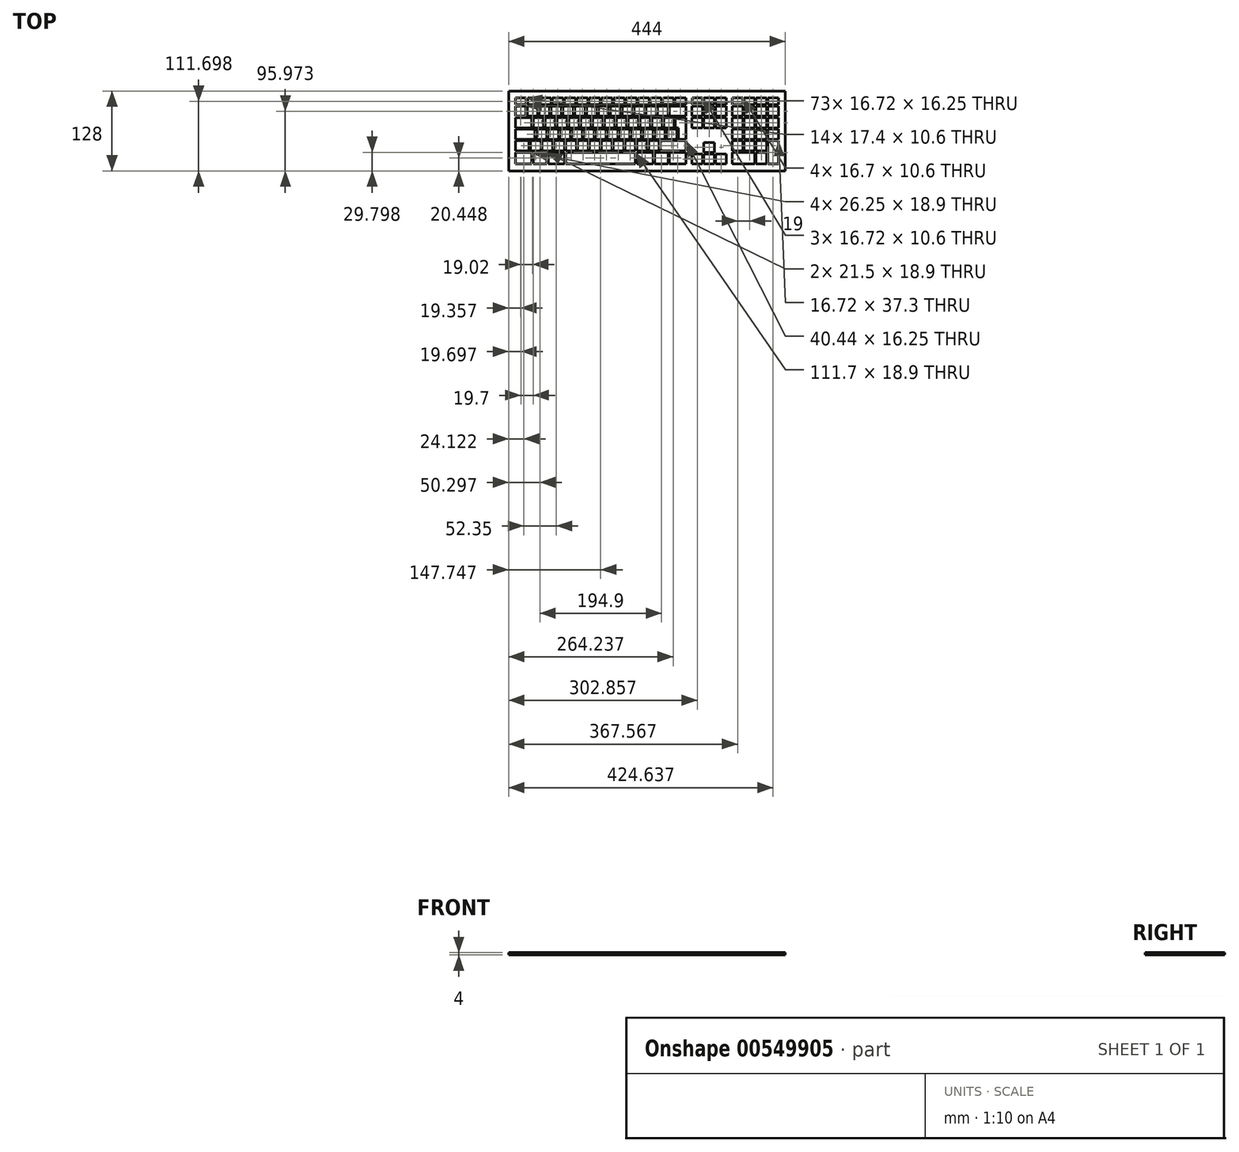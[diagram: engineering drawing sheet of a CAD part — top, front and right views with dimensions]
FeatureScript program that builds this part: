
annotation { "Feature Type Name" : "Feature", "Feature Type Description" : "" }
export const myFeature = defineFeature(function(context is Context, id is Id, definition is map)
    precondition{}
    {
        {
            var Q0;
            Q0=qCreatedBy(makeId("Top.planeOp"),FACE);
            var sketch = newSketch(context, id + "F0", { "sketchPlane" : qUnion([Q0])});
            skLineSegment(sketch, "E0.bottom", {"start": v(-207.41, -87.25) * mm, "end": v(222.59, -87.25) * mm, "construction": true});
            skLineSegment(sketch, "E0.top", {"start": v(-207.41, -201.25) * mm, "end": v(222.59, -201.25) * mm, "construction": true});
            skLineSegment(sketch, "E0.left", {"start": v(-207.41, -87.25) * mm, "end": v(-207.41, -201.25) * mm, "construction": true});
            skLineSegment(sketch, "E0.right", {"start": v(222.59, -87.25) * mm, "end": v(222.59, -201.25) * mm, "construction": true});
            skLineSegment(sketch, "E1.bottom", {"start": v(-203.41, -91.25) * mm, "end": v(-186.01, -91.25) * mm});
            skLineSegment(sketch, "E1.top", {"start": v(-203.41, -101.85) * mm, "end": v(-186.01, -101.85) * mm});
            skLineSegment(sketch, "E1.left", {"start": v(-203.41, -91.25) * mm, "end": v(-203.41, -101.85) * mm});
            skLineSegment(sketch, "E1.right", {"start": v(-186.01, -91.25) * mm, "end": v(-186.01, -101.85) * mm});
            skPoint(sketch, "E1.middle", {"position": v(-194.71, -96.55) * mm});
            skLineSegment(sketch, "E2.1.0.0", {"start": v(-166.31, -91.25) * mm, "end": v(-166.31, -101.85) * mm});
            skPoint(sketch, "E2.1.0.1", {"position": v(-175.01, -96.55) * mm});
            skLineSegment(sketch, "E2.1.0.2", {"start": v(-183.71, -91.25) * mm, "end": v(-183.71, -101.85) * mm});
            skLineSegment(sketch, "E2.1.0.3", {"start": v(-183.71, -101.85) * mm, "end": v(-166.31, -101.85) * mm});
            skLineSegment(sketch, "E2.1.0.4", {"start": v(-183.71, -91.25) * mm, "end": v(-166.31, -91.25) * mm});
            skLineSegment(sketch, "E2.2.0.0", {"start": v(-146.61, -91.25) * mm, "end": v(-146.61, -101.85) * mm});
            skPoint(sketch, "E2.2.0.1", {"position": v(-155.31, -96.55) * mm});
            skLineSegment(sketch, "E2.2.0.2", {"start": v(-164.01, -91.25) * mm, "end": v(-164.01, -101.85) * mm});
            skLineSegment(sketch, "E2.2.0.3", {"start": v(-164.01, -101.85) * mm, "end": v(-146.61, -101.85) * mm});
            skLineSegment(sketch, "E2.2.0.4", {"start": v(-164.01, -91.25) * mm, "end": v(-146.61, -91.25) * mm});
            skLineSegment(sketch, "E2.3.0.0", {"start": v(-126.91, -91.25) * mm, "end": v(-126.91, -101.85) * mm});
            skPoint(sketch, "E2.3.0.1", {"position": v(-135.61, -96.55) * mm});
            skLineSegment(sketch, "E2.3.0.2", {"start": v(-144.31, -91.25) * mm, "end": v(-144.31, -101.85) * mm});
            skLineSegment(sketch, "E2.3.0.3", {"start": v(-144.31, -101.85) * mm, "end": v(-126.91, -101.85) * mm});
            skLineSegment(sketch, "E2.3.0.4", {"start": v(-144.31, -91.25) * mm, "end": v(-126.91, -91.25) * mm});
            skLineSegment(sketch, "E2.4.0.0", {"start": v(-107.21, -91.25) * mm, "end": v(-107.21, -101.85) * mm});
            skPoint(sketch, "E2.4.0.1", {"position": v(-115.91, -96.55) * mm});
            skLineSegment(sketch, "E2.4.0.2", {"start": v(-124.61, -91.25) * mm, "end": v(-124.61, -101.85) * mm});
            skLineSegment(sketch, "E2.4.0.3", {"start": v(-124.61, -101.85) * mm, "end": v(-107.21, -101.85) * mm});
            skLineSegment(sketch, "E2.4.0.4", {"start": v(-124.61, -91.25) * mm, "end": v(-107.21, -91.25) * mm});
            skLineSegment(sketch, "E2.5.0.0", {"start": v(-87.51, -91.25) * mm, "end": v(-87.51, -101.85) * mm});
            skPoint(sketch, "E2.5.0.1", {"position": v(-96.21, -96.55) * mm});
            skLineSegment(sketch, "E2.5.0.2", {"start": v(-104.91, -91.25) * mm, "end": v(-104.91, -101.85) * mm});
            skLineSegment(sketch, "E2.5.0.3", {"start": v(-104.91, -101.85) * mm, "end": v(-87.51, -101.85) * mm});
            skLineSegment(sketch, "E2.5.0.4", {"start": v(-104.91, -91.25) * mm, "end": v(-87.51, -91.25) * mm});
            skLineSegment(sketch, "E2.6.0.0", {"start": v(-67.81, -91.25) * mm, "end": v(-67.81, -101.85) * mm});
            skPoint(sketch, "E2.6.0.1", {"position": v(-76.51, -96.55) * mm});
            skLineSegment(sketch, "E2.6.0.2", {"start": v(-85.21, -91.25) * mm, "end": v(-85.21, -101.85) * mm});
            skLineSegment(sketch, "E2.6.0.3", {"start": v(-85.21, -101.85) * mm, "end": v(-67.81, -101.85) * mm});
            skLineSegment(sketch, "E2.6.0.4", {"start": v(-85.21, -91.25) * mm, "end": v(-67.81, -91.25) * mm});
            skLineSegment(sketch, "E2.7.0.0", {"start": v(-48.11, -91.25) * mm, "end": v(-48.11, -101.85) * mm});
            skPoint(sketch, "E2.7.0.1", {"position": v(-56.81, -96.55) * mm});
            skLineSegment(sketch, "E2.7.0.2", {"start": v(-65.51, -91.25) * mm, "end": v(-65.51, -101.85) * mm});
            skLineSegment(sketch, "E2.7.0.3", {"start": v(-65.51, -101.85) * mm, "end": v(-48.11, -101.85) * mm});
            skLineSegment(sketch, "E2.7.0.4", {"start": v(-65.51, -91.25) * mm, "end": v(-48.11, -91.25) * mm});
            skLineSegment(sketch, "E2.8.0.0", {"start": v(-28.41, -91.25) * mm, "end": v(-28.41, -101.85) * mm});
            skPoint(sketch, "E2.8.0.1", {"position": v(-37.11, -96.55) * mm});
            skLineSegment(sketch, "E2.8.0.2", {"start": v(-45.81, -91.25) * mm, "end": v(-45.81, -101.85) * mm});
            skLineSegment(sketch, "E2.8.0.3", {"start": v(-45.81, -101.85) * mm, "end": v(-28.41, -101.85) * mm});
            skLineSegment(sketch, "E2.8.0.4", {"start": v(-45.81, -91.25) * mm, "end": v(-28.41, -91.25) * mm});
            skLineSegment(sketch, "E2.9.0.0", {"start": v(-8.71, -91.25) * mm, "end": v(-8.71, -101.85) * mm});
            skPoint(sketch, "E2.9.0.1", {"position": v(-17.41, -96.55) * mm});
            skLineSegment(sketch, "E2.9.0.2", {"start": v(-26.11, -91.25) * mm, "end": v(-26.11, -101.85) * mm});
            skLineSegment(sketch, "E2.9.0.3", {"start": v(-26.11, -101.85) * mm, "end": v(-8.71, -101.85) * mm});
            skLineSegment(sketch, "E2.9.0.4", {"start": v(-26.11, -91.25) * mm, "end": v(-8.71, -91.25) * mm});
            skLineSegment(sketch, "E2.10.0.0", {"start": v(10.99, -91.25) * mm, "end": v(10.99, -101.85) * mm});
            skPoint(sketch, "E2.10.0.1", {"position": v(2.29, -96.55) * mm});
            skLineSegment(sketch, "E2.10.0.2", {"start": v(-6.41, -91.25) * mm, "end": v(-6.41, -101.85) * mm});
            skLineSegment(sketch, "E2.10.0.3", {"start": v(-6.41, -101.85) * mm, "end": v(10.99, -101.85) * mm});
            skLineSegment(sketch, "E2.10.0.4", {"start": v(-6.41, -91.25) * mm, "end": v(10.99, -91.25) * mm});
            skLineSegment(sketch, "E2.11.0.0", {"start": v(30.69, -91.25) * mm, "end": v(30.69, -101.85) * mm});
            skPoint(sketch, "E2.11.0.1", {"position": v(21.99, -96.55) * mm});
            skLineSegment(sketch, "E2.11.0.2", {"start": v(13.29, -91.25) * mm, "end": v(13.29, -101.85) * mm});
            skLineSegment(sketch, "E2.11.0.3", {"start": v(13.29, -101.85) * mm, "end": v(30.69, -101.85) * mm});
            skLineSegment(sketch, "E2.11.0.4", {"start": v(13.29, -91.25) * mm, "end": v(30.69, -91.25) * mm});
            skLineSegment(sketch, "E2.12.0.0", {"start": v(50.39, -91.25) * mm, "end": v(50.39, -101.85) * mm});
            skPoint(sketch, "E2.12.0.1", {"position": v(41.69, -96.55) * mm});
            skLineSegment(sketch, "E2.12.0.2", {"start": v(32.99, -91.25) * mm, "end": v(32.99, -101.85) * mm});
            skLineSegment(sketch, "E2.12.0.3", {"start": v(32.99, -101.85) * mm, "end": v(50.39, -101.85) * mm});
            skLineSegment(sketch, "E2.12.0.4", {"start": v(32.99, -91.25) * mm, "end": v(50.39, -91.25) * mm});
            skLineSegment(sketch, "E2.13.0.0", {"start": v(70.09, -91.25) * mm, "end": v(70.09, -101.85) * mm});
            skPoint(sketch, "E2.13.0.1", {"position": v(61.39, -96.55) * mm});
            skLineSegment(sketch, "E2.13.0.2", {"start": v(52.69, -91.25) * mm, "end": v(52.69, -101.85) * mm});
            skLineSegment(sketch, "E2.13.0.3", {"start": v(52.69, -101.85) * mm, "end": v(70.09, -101.85) * mm});
            skLineSegment(sketch, "E2.13.0.4", {"start": v(52.69, -91.25) * mm, "end": v(70.09, -91.25) * mm});
            skLineSegment(sketch, "E3.bottom", {"start": v(80.09, -91.25) * mm, "end": v(96.8, -91.25) * mm});
            skLineSegment(sketch, "E3.top", {"start": v(80.09, -101.85) * mm, "end": v(96.8, -101.85) * mm});
            skLineSegment(sketch, "E3.left", {"start": v(80.09, -91.25) * mm, "end": v(80.09, -101.85) * mm});
            skLineSegment(sketch, "E3.right", {"start": v(96.8, -91.25) * mm, "end": v(96.8, -101.85) * mm});
            skPoint(sketch, "E3.middle", {"position": v(88.45, -96.55) * mm});
            skLineSegment(sketch, "E4.1.0.0", {"start": v(115.8, -91.25) * mm, "end": v(115.8, -101.85) * mm});
            skLineSegment(sketch, "E4.1.0.1", {"start": v(99.09, -91.25) * mm, "end": v(99.09, -101.85) * mm});
            skLineSegment(sketch, "E4.1.0.2", {"start": v(99.09, -91.25) * mm, "end": v(115.8, -91.25) * mm});
            skPoint(sketch, "E4.1.0.3", {"position": v(107.45, -96.55) * mm});
            skLineSegment(sketch, "E4.1.0.4", {"start": v(99.09, -101.85) * mm, "end": v(115.8, -101.85) * mm});
            skLineSegment(sketch, "E4.2.0.0", {"start": v(134.8, -91.25) * mm, "end": v(134.8, -101.85) * mm});
            skLineSegment(sketch, "E4.2.0.1", {"start": v(118.09, -91.25) * mm, "end": v(118.09, -101.85) * mm});
            skLineSegment(sketch, "E4.2.0.2", {"start": v(118.09, -91.25) * mm, "end": v(134.8, -91.25) * mm});
            skPoint(sketch, "E4.2.0.3", {"position": v(126.45, -96.55) * mm});
            skLineSegment(sketch, "E4.2.0.4", {"start": v(118.09, -101.85) * mm, "end": v(134.8, -101.85) * mm});
            skLineSegment(sketch, "E5.bottom", {"start": v(144.8, -91.25) * mm, "end": v(161.5, -91.25) * mm});
            skLineSegment(sketch, "E5.top", {"start": v(144.8, -101.85) * mm, "end": v(161.5, -101.85) * mm});
            skLineSegment(sketch, "E5.left", {"start": v(144.8, -91.25) * mm, "end": v(144.8, -101.85) * mm});
            skLineSegment(sketch, "E5.right", {"start": v(161.5, -91.25) * mm, "end": v(161.5, -101.85) * mm});
            skPoint(sketch, "E5.middle", {"position": v(153.16, -96.55) * mm});
            skLineSegment(sketch, "E6.1.0.0", {"start": v(180.5, -91.25) * mm, "end": v(180.5, -101.85) * mm});
            skLineSegment(sketch, "E6.1.0.1", {"start": v(163.8, -91.25) * mm, "end": v(180.5, -91.25) * mm});
            skLineSegment(sketch, "E6.1.0.2", {"start": v(163.8, -101.85) * mm, "end": v(180.5, -101.85) * mm});
            skLineSegment(sketch, "E6.1.0.3", {"start": v(163.8, -91.25) * mm, "end": v(163.8, -101.85) * mm});
            skPoint(sketch, "E6.1.0.4", {"position": v(172.16, -96.55) * mm});
            skLineSegment(sketch, "E6.2.0.0", {"start": v(199.5, -91.25) * mm, "end": v(199.5, -101.85) * mm});
            skLineSegment(sketch, "E6.2.0.1", {"start": v(182.8, -91.25) * mm, "end": v(199.5, -91.25) * mm});
            skLineSegment(sketch, "E6.2.0.2", {"start": v(182.8, -101.85) * mm, "end": v(199.5, -101.85) * mm});
            skLineSegment(sketch, "E6.2.0.3", {"start": v(182.8, -91.25) * mm, "end": v(182.8, -101.85) * mm});
            skPoint(sketch, "E6.2.0.4", {"position": v(191.16, -96.55) * mm});
            skLineSegment(sketch, "E6.3.0.0", {"start": v(218.5, -91.25) * mm, "end": v(218.5, -101.85) * mm});
            skLineSegment(sketch, "E6.3.0.1", {"start": v(201.8, -91.25) * mm, "end": v(218.5, -91.25) * mm});
            skLineSegment(sketch, "E6.3.0.2", {"start": v(201.8, -101.85) * mm, "end": v(218.5, -101.85) * mm});
            skLineSegment(sketch, "E6.3.0.3", {"start": v(201.8, -91.25) * mm, "end": v(201.8, -101.85) * mm});
            skPoint(sketch, "E6.3.0.4", {"position": v(210.16, -96.55) * mm});
            skLineSegment(sketch, "E7.bottom", {"start": v(-203.41, -104.15) * mm, "end": v(-186.7, -104.15) * mm});
            skLineSegment(sketch, "E7.top", {"start": v(-203.41, -120.4) * mm, "end": v(-186.7, -120.4) * mm});
            skLineSegment(sketch, "E7.left", {"start": v(-203.41, -104.15) * mm, "end": v(-203.41, -120.4) * mm});
            skLineSegment(sketch, "E7.right", {"start": v(-186.7, -104.15) * mm, "end": v(-186.7, -120.4) * mm});
            skPoint(sketch, "E7.middle", {"position": v(-195.05, -112.28) * mm});
            skPoint(sketch, "E8.1.0.0", {"position": v(-176.03, -112.28) * mm});
            skLineSegment(sketch, "E8.1.0.1", {"start": v(-167.67, -104.15) * mm, "end": v(-167.67, -120.4) * mm});
            skLineSegment(sketch, "E8.1.0.2", {"start": v(-184.4, -104.15) * mm, "end": v(-167.67, -104.15) * mm});
            skLineSegment(sketch, "E8.1.0.3", {"start": v(-184.4, -104.15) * mm, "end": v(-184.4, -120.4) * mm});
            skLineSegment(sketch, "E8.1.0.4", {"start": v(-184.4, -120.4) * mm, "end": v(-167.67, -120.4) * mm});
            skPoint(sketch, "E8.2.0.0", {"position": v(-157.01, -112.28) * mm});
            skLineSegment(sketch, "E8.2.0.1", {"start": v(-148.65, -104.15) * mm, "end": v(-148.65, -120.4) * mm});
            skLineSegment(sketch, "E8.2.0.2", {"start": v(-165.37, -104.15) * mm, "end": v(-148.65, -104.15) * mm});
            skLineSegment(sketch, "E8.2.0.3", {"start": v(-165.37, -104.15) * mm, "end": v(-165.37, -120.4) * mm});
            skLineSegment(sketch, "E8.2.0.4", {"start": v(-165.37, -120.4) * mm, "end": v(-148.65, -120.4) * mm});
            skPoint(sketch, "E8.3.0.0", {"position": v(-138, -112.28) * mm});
            skLineSegment(sketch, "E8.3.0.1", {"start": v(-129.63, -104.15) * mm, "end": v(-129.63, -120.4) * mm});
            skLineSegment(sketch, "E8.3.0.2", {"start": v(-146.35, -104.15) * mm, "end": v(-129.63, -104.15) * mm});
            skLineSegment(sketch, "E8.3.0.3", {"start": v(-146.35, -104.15) * mm, "end": v(-146.35, -120.4) * mm});
            skLineSegment(sketch, "E8.3.0.4", {"start": v(-146.35, -120.4) * mm, "end": v(-129.63, -120.4) * mm});
            skPoint(sketch, "E8.4.0.0", {"position": v(-118.97, -112.28) * mm});
            skLineSegment(sketch, "E8.4.0.1", {"start": v(-110.61, -104.15) * mm, "end": v(-110.61, -120.4) * mm});
            skLineSegment(sketch, "E8.4.0.2", {"start": v(-127.33, -104.15) * mm, "end": v(-110.61, -104.15) * mm});
            skLineSegment(sketch, "E8.4.0.3", {"start": v(-127.33, -104.15) * mm, "end": v(-127.33, -120.4) * mm});
            skLineSegment(sketch, "E8.4.0.4", {"start": v(-127.33, -120.4) * mm, "end": v(-110.61, -120.4) * mm});
            skPoint(sketch, "E8.5.0.0", {"position": v(-99.95, -112.28) * mm});
            skLineSegment(sketch, "E8.5.0.1", {"start": v(-91.6, -104.15) * mm, "end": v(-91.6, -120.4) * mm});
            skLineSegment(sketch, "E8.5.0.2", {"start": v(-108.31, -104.15) * mm, "end": v(-91.6, -104.15) * mm});
            skLineSegment(sketch, "E8.5.0.3", {"start": v(-108.31, -104.15) * mm, "end": v(-108.31, -120.4) * mm});
            skLineSegment(sketch, "E8.5.0.4", {"start": v(-108.31, -120.4) * mm, "end": v(-91.6, -120.4) * mm});
            skPoint(sketch, "E8.6.0.0", {"position": v(-80.93, -112.28) * mm});
            skLineSegment(sketch, "E8.6.0.1", {"start": v(-72.57, -104.15) * mm, "end": v(-72.57, -120.4) * mm});
            skLineSegment(sketch, "E8.6.0.2", {"start": v(-89.3, -104.15) * mm, "end": v(-72.57, -104.15) * mm});
            skLineSegment(sketch, "E8.6.0.3", {"start": v(-89.3, -104.15) * mm, "end": v(-89.3, -120.4) * mm});
            skLineSegment(sketch, "E8.6.0.4", {"start": v(-89.3, -120.4) * mm, "end": v(-72.57, -120.4) * mm});
            skPoint(sketch, "E8.7.0.0", {"position": v(-61.91, -112.28) * mm});
            skLineSegment(sketch, "E8.7.0.1", {"start": v(-53.55, -104.15) * mm, "end": v(-53.55, -120.4) * mm});
            skLineSegment(sketch, "E8.7.0.2", {"start": v(-70.27, -104.15) * mm, "end": v(-53.55, -104.15) * mm});
            skLineSegment(sketch, "E8.7.0.3", {"start": v(-70.27, -104.15) * mm, "end": v(-70.27, -120.4) * mm});
            skLineSegment(sketch, "E8.7.0.4", {"start": v(-70.27, -120.4) * mm, "end": v(-53.55, -120.4) * mm});
            skPoint(sketch, "E8.8.0.0", {"position": v(-42.9, -112.28) * mm});
            skLineSegment(sketch, "E8.8.0.1", {"start": v(-34.53, -104.15) * mm, "end": v(-34.53, -120.4) * mm});
            skLineSegment(sketch, "E8.8.0.2", {"start": v(-51.25, -104.15) * mm, "end": v(-34.53, -104.15) * mm});
            skLineSegment(sketch, "E8.8.0.3", {"start": v(-51.25, -104.15) * mm, "end": v(-51.25, -120.4) * mm});
            skLineSegment(sketch, "E8.8.0.4", {"start": v(-51.25, -120.4) * mm, "end": v(-34.53, -120.4) * mm});
            skPoint(sketch, "E8.9.0.0", {"position": v(-23.87, -112.28) * mm});
            skLineSegment(sketch, "E8.9.0.1", {"start": v(-15.51, -104.15) * mm, "end": v(-15.51, -120.4) * mm});
            skLineSegment(sketch, "E8.9.0.2", {"start": v(-32.23, -104.15) * mm, "end": v(-15.51, -104.15) * mm});
            skLineSegment(sketch, "E8.9.0.3", {"start": v(-32.23, -104.15) * mm, "end": v(-32.23, -120.4) * mm});
            skLineSegment(sketch, "E8.9.0.4", {"start": v(-32.23, -120.4) * mm, "end": v(-15.51, -120.4) * mm});
            skPoint(sketch, "E8.10.0.0", {"position": v(-4.85, -112.28) * mm});
            skLineSegment(sketch, "E8.10.0.1", {"start": v(3.5, -104.15) * mm, "end": v(3.5, -120.4) * mm});
            skLineSegment(sketch, "E8.10.0.2", {"start": v(-13.21, -104.15) * mm, "end": v(3.5, -104.15) * mm});
            skLineSegment(sketch, "E8.10.0.3", {"start": v(-13.21, -104.15) * mm, "end": v(-13.21, -120.4) * mm});
            skLineSegment(sketch, "E8.10.0.4", {"start": v(-13.21, -120.4) * mm, "end": v(3.5, -120.4) * mm});
            skPoint(sketch, "E8.11.0.0", {"position": v(14.17, -112.28) * mm});
            skLineSegment(sketch, "E8.11.0.1", {"start": v(22.53, -104.15) * mm, "end": v(22.53, -120.4) * mm});
            skLineSegment(sketch, "E8.11.0.2", {"start": v(5.8, -104.15) * mm, "end": v(22.53, -104.15) * mm});
            skLineSegment(sketch, "E8.11.0.3", {"start": v(5.8, -104.15) * mm, "end": v(5.8, -120.4) * mm});
            skLineSegment(sketch, "E8.11.0.4", {"start": v(5.8, -120.4) * mm, "end": v(22.53, -120.4) * mm});
            skPoint(sketch, "E8.12.0.0", {"position": v(33.19, -112.28) * mm});
            skLineSegment(sketch, "E8.12.0.1", {"start": v(41.55, -104.15) * mm, "end": v(41.55, -120.4) * mm});
            skLineSegment(sketch, "E8.12.0.2", {"start": v(24.83, -104.15) * mm, "end": v(41.55, -104.15) * mm});
            skLineSegment(sketch, "E8.12.0.3", {"start": v(24.83, -104.15) * mm, "end": v(24.83, -120.4) * mm});
            skLineSegment(sketch, "E8.12.0.4", {"start": v(24.83, -120.4) * mm, "end": v(41.55, -120.4) * mm});
            skLineSegment(sketch, "E9.bottom", {"start": v(43.85, -104.15) * mm, "end": v(70.05, -104.15) * mm});
            skLineSegment(sketch, "E9.top", {"start": v(43.85, -120.4) * mm, "end": v(70.05, -120.4) * mm});
            skLineSegment(sketch, "E9.left", {"start": v(43.85, -104.15) * mm, "end": v(43.85, -120.4) * mm});
            skLineSegment(sketch, "E9.right", {"start": v(70.05, -104.15) * mm, "end": v(70.05, -120.4) * mm});
            skPoint(sketch, "E9.middle", {"position": v(56.95, -112.28) * mm});
            skLineSegment(sketch, "E10.bottom", {"start": v(80.05, -104.15) * mm, "end": v(96.77, -104.15) * mm});
            skLineSegment(sketch, "E10.top", {"start": v(80.05, -120.4) * mm, "end": v(96.77, -120.4) * mm});
            skLineSegment(sketch, "E10.left", {"start": v(80.05, -104.15) * mm, "end": v(80.05, -120.4) * mm});
            skLineSegment(sketch, "E10.right", {"start": v(96.77, -104.15) * mm, "end": v(96.77, -120.4) * mm});
            skPoint(sketch, "E10.middle", {"position": v(88.4, -112.28) * mm});
            skPoint(sketch, "E11.1.0.0", {"position": v(107.43, -112.28) * mm});
            skLineSegment(sketch, "E11.1.0.1", {"start": v(99.07, -120.4) * mm, "end": v(115.79, -120.4) * mm});
            skLineSegment(sketch, "E11.1.0.2", {"start": v(115.79, -104.15) * mm, "end": v(115.79, -120.4) * mm});
            skLineSegment(sketch, "E11.1.0.3", {"start": v(99.07, -104.15) * mm, "end": v(115.79, -104.15) * mm});
            skLineSegment(sketch, "E11.1.0.4", {"start": v(99.07, -104.15) * mm, "end": v(99.07, -120.4) * mm});
            skPoint(sketch, "E11.2.0.0", {"position": v(126.45, -112.28) * mm});
            skLineSegment(sketch, "E11.2.0.1", {"start": v(118.09, -120.4) * mm, "end": v(134.8, -120.4) * mm});
            skLineSegment(sketch, "E11.2.0.2", {"start": v(134.8, -104.15) * mm, "end": v(134.8, -120.4) * mm});
            skLineSegment(sketch, "E11.2.0.3", {"start": v(118.09, -104.15) * mm, "end": v(134.8, -104.15) * mm});
            skLineSegment(sketch, "E11.2.0.4", {"start": v(118.09, -104.15) * mm, "end": v(118.09, -120.4) * mm});
            skLineSegment(sketch, "E12.bottom", {"start": v(80.05, -122.7) * mm, "end": v(96.77, -122.7) * mm});
            skLineSegment(sketch, "E12.top", {"start": v(80.05, -138.95) * mm, "end": v(96.77, -138.95) * mm});
            skLineSegment(sketch, "E12.left", {"start": v(80.05, -122.7) * mm, "end": v(80.05, -138.95) * mm});
            skLineSegment(sketch, "E12.right", {"start": v(96.77, -122.7) * mm, "end": v(96.77, -138.95) * mm});
            skPoint(sketch, "E12.middle", {"position": v(88.4, -130.83) * mm});
            skLineSegment(sketch, "E13.1.0.0", {"start": v(99.07, -138.95) * mm, "end": v(115.79, -138.95) * mm});
            skLineSegment(sketch, "E13.1.0.1", {"start": v(99.07, -122.7) * mm, "end": v(115.79, -122.7) * mm});
            skLineSegment(sketch, "E13.1.0.2", {"start": v(99.07, -122.7) * mm, "end": v(99.07, -138.95) * mm});
            skPoint(sketch, "E13.1.0.3", {"position": v(107.43, -130.83) * mm});
            skLineSegment(sketch, "E13.1.0.4", {"start": v(115.79, -122.7) * mm, "end": v(115.79, -138.95) * mm});
            skLineSegment(sketch, "E13.2.0.0", {"start": v(118.09, -138.95) * mm, "end": v(134.8, -138.95) * mm});
            skLineSegment(sketch, "E13.2.0.1", {"start": v(118.09, -122.7) * mm, "end": v(134.8, -122.7) * mm});
            skLineSegment(sketch, "E13.2.0.2", {"start": v(118.09, -122.7) * mm, "end": v(118.09, -138.95) * mm});
            skPoint(sketch, "E13.2.0.3", {"position": v(126.45, -130.83) * mm});
            skLineSegment(sketch, "E13.2.0.4", {"start": v(134.8, -122.7) * mm, "end": v(134.8, -138.95) * mm});
            skPoint(sketch, "E14.1.0.0", {"position": v(153.17, -112.28) * mm});
            skLineSegment(sketch, "E14.1.0.1", {"start": v(144.8, -104.15) * mm, "end": v(161.53, -104.15) * mm});
            skLineSegment(sketch, "E14.1.0.3", {"start": v(161.53, -104.15) * mm, "end": v(161.53, -120.4) * mm});
            skLineSegment(sketch, "E14.1.0.4", {"start": v(144.8, -120.4) * mm, "end": v(161.53, -120.4) * mm});
            skLineSegment(sketch, "E14.1.0.7", {"start": v(144.8, -104.15) * mm, "end": v(144.8, -120.4) * mm});
            skLineSegment(sketch, "E15.0.1.0", {"start": v(144.8, -122.7) * mm, "end": v(144.8, -138.95) * mm});
            skPoint(sketch, "E15.0.1.1", {"position": v(153.17, -130.83) * mm});
            skLineSegment(sketch, "E15.0.1.2", {"start": v(144.8, -122.7) * mm, "end": v(161.53, -122.7) * mm});
            skLineSegment(sketch, "E15.0.1.3", {"start": v(161.53, -122.7) * mm, "end": v(161.53, -138.95) * mm});
            skLineSegment(sketch, "E15.0.1.4", {"start": v(144.8, -138.95) * mm, "end": v(161.53, -138.95) * mm});
            skLineSegment(sketch, "E15.0.2.0", {"start": v(144.8, -141.25) * mm, "end": v(144.8, -157.5) * mm});
            skPoint(sketch, "E15.0.2.1", {"position": v(153.17, -149.38) * mm});
            skLineSegment(sketch, "E15.0.2.2", {"start": v(144.8, -141.25) * mm, "end": v(161.53, -141.25) * mm});
            skLineSegment(sketch, "E15.0.2.3", {"start": v(161.53, -141.25) * mm, "end": v(161.53, -157.5) * mm});
            skLineSegment(sketch, "E15.0.2.4", {"start": v(144.8, -157.5) * mm, "end": v(161.53, -157.5) * mm});
            skLineSegment(sketch, "E15.0.3.0", {"start": v(144.8, -159.8) * mm, "end": v(144.8, -176.05) * mm});
            skPoint(sketch, "E15.0.3.1", {"position": v(153.17, -167.93) * mm});
            skLineSegment(sketch, "E15.0.3.2", {"start": v(144.8, -159.8) * mm, "end": v(161.53, -159.8) * mm});
            skLineSegment(sketch, "E15.0.3.3", {"start": v(161.53, -159.8) * mm, "end": v(161.53, -176.05) * mm});
            skLineSegment(sketch, "E15.0.3.4", {"start": v(144.8, -176.05) * mm, "end": v(161.53, -176.05) * mm});
            skLineSegment(sketch, "E15.1.0.0", {"start": v(163.83, -104.15) * mm, "end": v(163.83, -120.4) * mm});
            skPoint(sketch, "E15.1.0.1", {"position": v(172.19, -112.28) * mm});
            skLineSegment(sketch, "E15.1.0.2", {"start": v(163.83, -104.15) * mm, "end": v(180.55, -104.15) * mm});
            skLineSegment(sketch, "E15.1.0.3", {"start": v(180.55, -104.15) * mm, "end": v(180.55, -120.4) * mm});
            skLineSegment(sketch, "E15.1.0.4", {"start": v(163.83, -120.4) * mm, "end": v(180.55, -120.4) * mm});
            skLineSegment(sketch, "E15.1.1.0", {"start": v(163.83, -122.7) * mm, "end": v(163.83, -138.95) * mm});
            skPoint(sketch, "E15.1.1.1", {"position": v(172.19, -130.83) * mm});
            skLineSegment(sketch, "E15.1.1.2", {"start": v(163.83, -122.7) * mm, "end": v(180.55, -122.7) * mm});
            skLineSegment(sketch, "E15.1.1.3", {"start": v(180.55, -122.7) * mm, "end": v(180.55, -138.95) * mm});
            skLineSegment(sketch, "E15.1.1.4", {"start": v(163.83, -138.95) * mm, "end": v(180.55, -138.95) * mm});
            skLineSegment(sketch, "E15.1.2.0", {"start": v(163.83, -141.25) * mm, "end": v(163.83, -157.5) * mm});
            skPoint(sketch, "E15.1.2.1", {"position": v(172.19, -149.38) * mm});
            skLineSegment(sketch, "E15.1.2.2", {"start": v(163.83, -141.25) * mm, "end": v(180.55, -141.25) * mm});
            skLineSegment(sketch, "E15.1.2.3", {"start": v(180.55, -141.25) * mm, "end": v(180.55, -157.5) * mm});
            skLineSegment(sketch, "E15.1.2.4", {"start": v(163.83, -157.5) * mm, "end": v(180.55, -157.5) * mm});
            skLineSegment(sketch, "E15.1.3.0", {"start": v(163.83, -159.8) * mm, "end": v(163.83, -176.05) * mm});
            skPoint(sketch, "E15.1.3.1", {"position": v(172.19, -167.93) * mm});
            skLineSegment(sketch, "E15.1.3.2", {"start": v(163.83, -159.8) * mm, "end": v(180.55, -159.8) * mm});
            skLineSegment(sketch, "E15.1.3.3", {"start": v(180.55, -159.8) * mm, "end": v(180.55, -176.05) * mm});
            skLineSegment(sketch, "E15.1.3.4", {"start": v(163.83, -176.05) * mm, "end": v(180.55, -176.05) * mm});
            skLineSegment(sketch, "E15.2.0.0", {"start": v(182.85, -104.15) * mm, "end": v(182.85, -120.4) * mm});
            skPoint(sketch, "E15.2.0.1", {"position": v(191.2, -112.28) * mm});
            skLineSegment(sketch, "E15.2.0.2", {"start": v(182.85, -104.15) * mm, "end": v(199.57, -104.15) * mm});
            skLineSegment(sketch, "E15.2.0.3", {"start": v(199.57, -104.15) * mm, "end": v(199.57, -120.4) * mm});
            skLineSegment(sketch, "E15.2.0.4", {"start": v(182.85, -120.4) * mm, "end": v(199.57, -120.4) * mm});
            skLineSegment(sketch, "E15.2.1.0", {"start": v(182.85, -122.7) * mm, "end": v(182.85, -138.95) * mm});
            skPoint(sketch, "E15.2.1.1", {"position": v(191.2, -130.83) * mm});
            skLineSegment(sketch, "E15.2.1.2", {"start": v(182.85, -122.7) * mm, "end": v(199.57, -122.7) * mm});
            skLineSegment(sketch, "E15.2.1.3", {"start": v(199.57, -122.7) * mm, "end": v(199.57, -138.95) * mm});
            skLineSegment(sketch, "E15.2.1.4", {"start": v(182.85, -138.95) * mm, "end": v(199.57, -138.95) * mm});
            skLineSegment(sketch, "E15.2.2.0", {"start": v(182.85, -141.25) * mm, "end": v(182.85, -157.5) * mm});
            skPoint(sketch, "E15.2.2.1", {"position": v(191.2, -149.38) * mm});
            skLineSegment(sketch, "E15.2.2.2", {"start": v(182.85, -141.25) * mm, "end": v(199.57, -141.25) * mm});
            skLineSegment(sketch, "E15.2.2.3", {"start": v(199.57, -141.25) * mm, "end": v(199.57, -157.5) * mm});
            skLineSegment(sketch, "E15.2.2.4", {"start": v(182.85, -157.5) * mm, "end": v(199.57, -157.5) * mm});
            skLineSegment(sketch, "E15.2.3.0", {"start": v(182.85, -159.8) * mm, "end": v(182.85, -176.05) * mm});
            skPoint(sketch, "E15.2.3.1", {"position": v(191.2, -167.93) * mm});
            skLineSegment(sketch, "E15.2.3.2", {"start": v(182.85, -159.8) * mm, "end": v(199.57, -159.8) * mm});
            skLineSegment(sketch, "E15.2.3.3", {"start": v(199.57, -159.8) * mm, "end": v(199.57, -176.05) * mm});
            skLineSegment(sketch, "E15.2.3.4", {"start": v(182.85, -176.05) * mm, "end": v(199.57, -176.05) * mm});
            skLineSegment(sketch, "E15.3.0.0", {"start": v(201.87, -104.15) * mm, "end": v(201.87, -120.4) * mm});
            skPoint(sketch, "E15.3.0.1", {"position": v(210.23, -112.28) * mm});
            skLineSegment(sketch, "E15.3.0.2", {"start": v(201.87, -104.15) * mm, "end": v(218.59, -104.15) * mm});
            skLineSegment(sketch, "E15.3.0.3", {"start": v(218.59, -104.15) * mm, "end": v(218.59, -120.4) * mm});
            skLineSegment(sketch, "E15.3.0.4", {"start": v(201.87, -120.4) * mm, "end": v(218.59, -120.4) * mm});
            skLineSegment(sketch, "E15.3.1.0", {"start": v(201.87, -122.7) * mm, "end": v(201.87, -138.95) * mm});
            skPoint(sketch, "E15.3.1.1", {"position": v(210.23, -130.83) * mm});
            skLineSegment(sketch, "E15.3.1.2", {"start": v(201.87, -122.7) * mm, "end": v(218.59, -122.7) * mm});
            skLineSegment(sketch, "E15.3.1.3", {"start": v(218.59, -122.7) * mm, "end": v(218.59, -138.95) * mm});
            skLineSegment(sketch, "E15.3.1.4", {"start": v(201.87, -138.95) * mm, "end": v(218.59, -138.95) * mm});
            skLineSegment(sketch, "E15.3.2.0", {"start": v(201.87, -141.25) * mm, "end": v(201.87, -157.5) * mm});
            skPoint(sketch, "E15.3.2.1", {"position": v(210.23, -149.38) * mm});
            skLineSegment(sketch, "E15.3.2.2", {"start": v(201.87, -141.25) * mm, "end": v(218.59, -141.25) * mm});
            skLineSegment(sketch, "E15.3.2.3", {"start": v(218.59, -141.25) * mm, "end": v(218.59, -157.5) * mm});
            skLineSegment(sketch, "E15.3.2.4", {"start": v(201.87, -157.5) * mm, "end": v(218.59, -157.5) * mm});
            skLineSegment(sketch, "E15.3.3.0", {"start": v(201.87, -159.8) * mm, "end": v(201.87, -197.1) * mm});
            skPoint(sketch, "E15.3.3.1", {"position": v(210.23, -178.45) * mm});
            skLineSegment(sketch, "E15.3.3.2", {"start": v(201.87, -159.8) * mm, "end": v(218.59, -159.8) * mm});
            skLineSegment(sketch, "E15.3.3.3", {"start": v(218.59, -159.8) * mm, "end": v(218.59, -197.1) * mm});
            skLineSegment(sketch, "E15.3.3.4", {"start": v(201.87, -197.1) * mm, "end": v(218.59, -197.1) * mm});
            skLineSegment(sketch, "E16.bottom", {"start": v(182.85, -178.35) * mm, "end": v(199.57, -178.35) * mm});
            skLineSegment(sketch, "E16.top", {"start": v(182.85, -197.16) * mm, "end": v(199.57, -197.16) * mm});
            skLineSegment(sketch, "E16.left", {"start": v(182.85, -178.35) * mm, "end": v(182.85, -197.16) * mm});
            skLineSegment(sketch, "E16.right", {"start": v(199.57, -178.35) * mm, "end": v(199.57, -197.16) * mm});
            skPoint(sketch, "E16.middle", {"position": v(191.2, -187.76) * mm});
            skLineSegment(sketch, "E17.bottom", {"start": v(144.8, -178.35) * mm, "end": v(180.55, -178.35) * mm});
            skLineSegment(sketch, "E17.top", {"start": v(144.8, -197.16) * mm, "end": v(180.55, -197.16) * mm});
            skLineSegment(sketch, "E17.left", {"start": v(144.8, -178.35) * mm, "end": v(144.8, -197.16) * mm});
            skLineSegment(sketch, "E17.right", {"start": v(180.55, -178.35) * mm, "end": v(180.55, -197.16) * mm});
            skPoint(sketch, "E17.middle", {"position": v(162.68, -187.76) * mm});
            skLineSegment(sketch, "E18.bottom", {"start": v(118.09, -181) * mm, "end": v(134.8, -181) * mm});
            skLineSegment(sketch, "E18.top", {"start": v(118.09, -197.25) * mm, "end": v(134.8, -197.25) * mm});
            skLineSegment(sketch, "E18.left", {"start": v(118.09, -181) * mm, "end": v(118.09, -197.25) * mm});
            skLineSegment(sketch, "E18.right", {"start": v(134.8, -181) * mm, "end": v(134.8, -197.25) * mm});
            skPoint(sketch, "E18.middle", {"position": v(126.45, -189.13) * mm});
            skPoint(sketch, "E19.1.0.0", {"position": v(107.43, -189.13) * mm});
            skLineSegment(sketch, "E19.1.0.1", {"start": v(99.07, -197.25) * mm, "end": v(115.79, -197.25) * mm});
            skLineSegment(sketch, "E19.1.0.2", {"start": v(99.07, -181) * mm, "end": v(115.79, -181) * mm});
            skLineSegment(sketch, "E19.1.0.3", {"start": v(115.79, -181) * mm, "end": v(115.79, -197.25) * mm});
            skLineSegment(sketch, "E19.1.0.4", {"start": v(99.07, -181) * mm, "end": v(99.07, -197.25) * mm});
            skPoint(sketch, "E19.2.0.0", {"position": v(88.4, -189.13) * mm});
            skLineSegment(sketch, "E19.2.0.1", {"start": v(80.05, -197.25) * mm, "end": v(96.77, -197.25) * mm});
            skLineSegment(sketch, "E19.2.0.2", {"start": v(80.05, -181) * mm, "end": v(96.77, -181) * mm});
            skLineSegment(sketch, "E19.2.0.3", {"start": v(96.77, -181) * mm, "end": v(96.77, -197.25) * mm});
            skLineSegment(sketch, "E19.2.0.4", {"start": v(80.05, -181) * mm, "end": v(80.05, -197.25) * mm});
            skLineSegment(sketch, "E20.0.1.0", {"start": v(99.07, -162.45) * mm, "end": v(115.79, -162.45) * mm});
            skLineSegment(sketch, "E20.0.1.1", {"start": v(99.07, -162.45) * mm, "end": v(99.07, -178.7) * mm});
            skLineSegment(sketch, "E20.0.1.2", {"start": v(115.79, -162.45) * mm, "end": v(115.79, -178.7) * mm});
            skPoint(sketch, "E20.0.1.3", {"position": v(107.43, -170.58) * mm});
            skLineSegment(sketch, "E20.0.1.4", {"start": v(99.07, -178.7) * mm, "end": v(115.79, -178.7) * mm});
            skLineSegment(sketch, "E21.bottom", {"start": v(-203.41, -122.7) * mm, "end": v(-177.16, -122.7) * mm});
            skLineSegment(sketch, "E21.top", {"start": v(-203.41, -138.95) * mm, "end": v(-177.16, -138.95) * mm});
            skLineSegment(sketch, "E21.left", {"start": v(-203.41, -122.7) * mm, "end": v(-203.41, -138.95) * mm});
            skLineSegment(sketch, "E21.right", {"start": v(-177.16, -122.7) * mm, "end": v(-177.16, -138.95) * mm});
            skPoint(sketch, "E21.middle", {"position": v(-190.29, -130.83) * mm});
            skLineSegment(sketch, "E22.bottom", {"start": v(-174.86, -122.7) * mm, "end": v(-158.14, -122.7) * mm});
            skLineSegment(sketch, "E22.top", {"start": v(-174.86, -138.95) * mm, "end": v(-158.14, -138.95) * mm});
            skLineSegment(sketch, "E22.left", {"start": v(-174.86, -122.7) * mm, "end": v(-174.86, -138.95) * mm});
            skLineSegment(sketch, "E22.right", {"start": v(-158.14, -122.7) * mm, "end": v(-158.14, -138.95) * mm});
            skPoint(sketch, "E22.middle", {"position": v(-166.5, -130.83) * mm});
            skLineSegment(sketch, "E23.1.0.0", {"start": v(-139.12, -122.7) * mm, "end": v(-139.12, -138.95) * mm});
            skLineSegment(sketch, "E23.1.0.1", {"start": v(-155.84, -122.7) * mm, "end": v(-155.84, -138.95) * mm});
            skLineSegment(sketch, "E23.1.0.2", {"start": v(-155.84, -122.7) * mm, "end": v(-139.12, -122.7) * mm});
            skPoint(sketch, "E23.1.0.3", {"position": v(-147.48, -130.83) * mm});
            skLineSegment(sketch, "E23.1.0.4", {"start": v(-155.84, -138.95) * mm, "end": v(-139.12, -138.95) * mm});
            skLineSegment(sketch, "E23.2.0.0", {"start": v(-120.1, -122.7) * mm, "end": v(-120.1, -138.95) * mm});
            skLineSegment(sketch, "E23.2.0.1", {"start": v(-136.82, -122.7) * mm, "end": v(-136.82, -138.95) * mm});
            skLineSegment(sketch, "E23.2.0.2", {"start": v(-136.82, -122.7) * mm, "end": v(-120.1, -122.7) * mm});
            skPoint(sketch, "E23.2.0.3", {"position": v(-128.46, -130.83) * mm});
            skLineSegment(sketch, "E23.2.0.4", {"start": v(-136.82, -138.95) * mm, "end": v(-120.1, -138.95) * mm});
            skLineSegment(sketch, "E23.3.0.0", {"start": v(-101.08, -122.7) * mm, "end": v(-101.08, -138.95) * mm});
            skLineSegment(sketch, "E23.3.0.1", {"start": v(-117.8, -122.7) * mm, "end": v(-117.8, -138.95) * mm});
            skLineSegment(sketch, "E23.3.0.2", {"start": v(-117.8, -122.7) * mm, "end": v(-101.08, -122.7) * mm});
            skPoint(sketch, "E23.3.0.3", {"position": v(-109.44, -130.83) * mm});
            skLineSegment(sketch, "E23.3.0.4", {"start": v(-117.8, -138.95) * mm, "end": v(-101.08, -138.95) * mm});
            skLineSegment(sketch, "E23.4.0.0", {"start": v(-82.06, -122.7) * mm, "end": v(-82.06, -138.95) * mm});
            skLineSegment(sketch, "E23.4.0.1", {"start": v(-98.78, -122.7) * mm, "end": v(-98.78, -138.95) * mm});
            skLineSegment(sketch, "E23.4.0.2", {"start": v(-98.78, -122.7) * mm, "end": v(-82.06, -122.7) * mm});
            skPoint(sketch, "E23.4.0.3", {"position": v(-90.42, -130.83) * mm});
            skLineSegment(sketch, "E23.4.0.4", {"start": v(-98.78, -138.95) * mm, "end": v(-82.06, -138.95) * mm});
            skLineSegment(sketch, "E23.5.0.0", {"start": v(-63.04, -122.7) * mm, "end": v(-63.04, -138.95) * mm});
            skLineSegment(sketch, "E23.5.0.1", {"start": v(-79.76, -122.7) * mm, "end": v(-79.76, -138.95) * mm});
            skLineSegment(sketch, "E23.5.0.2", {"start": v(-79.76, -122.7) * mm, "end": v(-63.04, -122.7) * mm});
            skPoint(sketch, "E23.5.0.3", {"position": v(-71.4, -130.83) * mm});
            skLineSegment(sketch, "E23.5.0.4", {"start": v(-79.76, -138.95) * mm, "end": v(-63.04, -138.95) * mm});
            skLineSegment(sketch, "E23.6.0.0", {"start": v(-44.02, -122.7) * mm, "end": v(-44.02, -138.95) * mm});
            skLineSegment(sketch, "E23.6.0.1", {"start": v(-60.74, -122.7) * mm, "end": v(-60.74, -138.95) * mm});
            skLineSegment(sketch, "E23.6.0.2", {"start": v(-60.74, -122.7) * mm, "end": v(-44.02, -122.7) * mm});
            skPoint(sketch, "E23.6.0.3", {"position": v(-52.38, -130.83) * mm});
            skLineSegment(sketch, "E23.6.0.4", {"start": v(-60.74, -138.95) * mm, "end": v(-44.02, -138.95) * mm});
            skLineSegment(sketch, "E23.7.0.0", {"start": v(-25, -122.7) * mm, "end": v(-25, -138.95) * mm});
            skLineSegment(sketch, "E23.7.0.1", {"start": v(-41.72, -122.7) * mm, "end": v(-41.72, -138.95) * mm});
            skLineSegment(sketch, "E23.7.0.2", {"start": v(-41.72, -122.7) * mm, "end": v(-25, -122.7) * mm});
            skPoint(sketch, "E23.7.0.3", {"position": v(-33.36, -130.83) * mm});
            skLineSegment(sketch, "E23.7.0.4", {"start": v(-41.72, -138.95) * mm, "end": v(-25, -138.95) * mm});
            skLineSegment(sketch, "E23.8.0.0", {"start": v(-5.98, -122.7) * mm, "end": v(-5.98, -138.95) * mm});
            skLineSegment(sketch, "E23.8.0.1", {"start": v(-22.7, -122.7) * mm, "end": v(-22.7, -138.95) * mm});
            skLineSegment(sketch, "E23.8.0.2", {"start": v(-22.7, -122.7) * mm, "end": v(-5.98, -122.7) * mm});
            skPoint(sketch, "E23.8.0.3", {"position": v(-14.34, -130.83) * mm});
            skLineSegment(sketch, "E23.8.0.4", {"start": v(-22.7, -138.95) * mm, "end": v(-5.98, -138.95) * mm});
            skLineSegment(sketch, "E23.9.0.0", {"start": v(13.04, -122.7) * mm, "end": v(13.04, -138.95) * mm});
            skLineSegment(sketch, "E23.9.0.1", {"start": v(-3.68, -122.7) * mm, "end": v(-3.68, -138.95) * mm});
            skLineSegment(sketch, "E23.9.0.2", {"start": v(-3.68, -122.7) * mm, "end": v(13.04, -122.7) * mm});
            skPoint(sketch, "E23.9.0.3", {"position": v(4.68, -130.83) * mm});
            skLineSegment(sketch, "E23.9.0.4", {"start": v(-3.68, -138.95) * mm, "end": v(13.04, -138.95) * mm});
            skLineSegment(sketch, "E23.10.0.0", {"start": v(32.06, -122.7) * mm, "end": v(32.06, -138.95) * mm});
            skLineSegment(sketch, "E23.10.0.1", {"start": v(15.34, -122.7) * mm, "end": v(15.34, -138.95) * mm});
            skLineSegment(sketch, "E23.10.0.2", {"start": v(15.34, -122.7) * mm, "end": v(32.06, -122.7) * mm});
            skPoint(sketch, "E23.10.0.3", {"position": v(23.7, -130.83) * mm});
            skLineSegment(sketch, "E23.10.0.4", {"start": v(15.34, -138.95) * mm, "end": v(32.06, -138.95) * mm});
            skLineSegment(sketch, "E23.11.0.0", {"start": v(51.08, -122.7) * mm, "end": v(51.08, -138.95) * mm});
            skLineSegment(sketch, "E23.11.0.1", {"start": v(34.36, -122.7) * mm, "end": v(34.36, -138.95) * mm});
            skLineSegment(sketch, "E23.11.0.2", {"start": v(34.36, -122.7) * mm, "end": v(51.08, -122.7) * mm});
            skPoint(sketch, "E23.11.0.3", {"position": v(42.72, -130.83) * mm});
            skLineSegment(sketch, "E23.11.0.4", {"start": v(34.36, -138.95) * mm, "end": v(51.08, -138.95) * mm});
            skLineSegment(sketch, "E24.bottom", {"start": v(-203.41, -141.25) * mm, "end": v(-172.41, -141.25) * mm});
            skLineSegment(sketch, "E24.top", {"start": v(-203.41, -157.5) * mm, "end": v(-172.41, -157.5) * mm});
            skLineSegment(sketch, "E24.left", {"start": v(-203.41, -141.25) * mm, "end": v(-203.41, -157.5) * mm});
            skLineSegment(sketch, "E24.right", {"start": v(-172.41, -141.25) * mm, "end": v(-172.41, -157.5) * mm});
            skPoint(sketch, "E24.middle", {"position": v(-187.91, -149.38) * mm});
            skLineSegment(sketch, "E25.bottom", {"start": v(-170.11, -141.25) * mm, "end": v(-153.4, -141.25) * mm});
            skLineSegment(sketch, "E25.top", {"start": v(-170.11, -157.5) * mm, "end": v(-153.4, -157.5) * mm});
            skLineSegment(sketch, "E25.left", {"start": v(-170.11, -141.25) * mm, "end": v(-170.11, -157.5) * mm});
            skLineSegment(sketch, "E25.right", {"start": v(-153.4, -141.25) * mm, "end": v(-153.4, -157.5) * mm});
            skPoint(sketch, "E25.middle", {"position": v(-161.75, -149.38) * mm});
            skLineSegment(sketch, "E26.1.0.0", {"start": v(-151.1, -157.5) * mm, "end": v(-134.37, -157.5) * mm});
            skPoint(sketch, "E26.1.0.1", {"position": v(-142.73, -149.38) * mm});
            skLineSegment(sketch, "E26.1.0.2", {"start": v(-151.1, -141.25) * mm, "end": v(-134.37, -141.25) * mm});
            skLineSegment(sketch, "E26.1.0.3", {"start": v(-134.37, -141.25) * mm, "end": v(-134.37, -157.5) * mm});
            skLineSegment(sketch, "E26.1.0.4", {"start": v(-151.1, -141.25) * mm, "end": v(-151.1, -157.5) * mm});
            skLineSegment(sketch, "E26.2.0.0", {"start": v(-132.07, -157.5) * mm, "end": v(-115.35, -157.5) * mm});
            skPoint(sketch, "E26.2.0.1", {"position": v(-123.71, -149.38) * mm});
            skLineSegment(sketch, "E26.2.0.2", {"start": v(-132.07, -141.25) * mm, "end": v(-115.35, -141.25) * mm});
            skLineSegment(sketch, "E26.2.0.3", {"start": v(-115.35, -141.25) * mm, "end": v(-115.35, -157.5) * mm});
            skLineSegment(sketch, "E26.2.0.4", {"start": v(-132.07, -141.25) * mm, "end": v(-132.07, -157.5) * mm});
            skLineSegment(sketch, "E26.3.0.0", {"start": v(-113.05, -157.5) * mm, "end": v(-96.33, -157.5) * mm});
            skPoint(sketch, "E26.3.0.1", {"position": v(-104.7, -149.38) * mm});
            skLineSegment(sketch, "E26.3.0.2", {"start": v(-113.05, -141.25) * mm, "end": v(-96.33, -141.25) * mm});
            skLineSegment(sketch, "E26.3.0.3", {"start": v(-96.33, -141.25) * mm, "end": v(-96.33, -157.5) * mm});
            skLineSegment(sketch, "E26.3.0.4", {"start": v(-113.05, -141.25) * mm, "end": v(-113.05, -157.5) * mm});
            skLineSegment(sketch, "E26.4.0.0", {"start": v(-94.03, -157.5) * mm, "end": v(-77.31, -157.5) * mm});
            skPoint(sketch, "E26.4.0.1", {"position": v(-85.67, -149.38) * mm});
            skLineSegment(sketch, "E26.4.0.2", {"start": v(-94.03, -141.25) * mm, "end": v(-77.31, -141.25) * mm});
            skLineSegment(sketch, "E26.4.0.3", {"start": v(-77.31, -141.25) * mm, "end": v(-77.31, -157.5) * mm});
            skLineSegment(sketch, "E26.4.0.4", {"start": v(-94.03, -141.25) * mm, "end": v(-94.03, -157.5) * mm});
            skLineSegment(sketch, "E26.5.0.0", {"start": v(-75.01, -157.5) * mm, "end": v(-58.3, -157.5) * mm});
            skPoint(sketch, "E26.5.0.1", {"position": v(-66.65, -149.38) * mm});
            skLineSegment(sketch, "E26.5.0.2", {"start": v(-75.01, -141.25) * mm, "end": v(-58.3, -141.25) * mm});
            skLineSegment(sketch, "E26.5.0.3", {"start": v(-58.3, -141.25) * mm, "end": v(-58.3, -157.5) * mm});
            skLineSegment(sketch, "E26.5.0.4", {"start": v(-75.01, -141.25) * mm, "end": v(-75.01, -157.5) * mm});
            skLineSegment(sketch, "E26.6.0.0", {"start": v(-56, -157.5) * mm, "end": v(-39.27, -157.5) * mm});
            skPoint(sketch, "E26.6.0.1", {"position": v(-47.63, -149.38) * mm});
            skLineSegment(sketch, "E26.6.0.2", {"start": v(-56, -141.25) * mm, "end": v(-39.27, -141.25) * mm});
            skLineSegment(sketch, "E26.6.0.3", {"start": v(-39.27, -141.25) * mm, "end": v(-39.27, -157.5) * mm});
            skLineSegment(sketch, "E26.6.0.4", {"start": v(-56, -141.25) * mm, "end": v(-56, -157.5) * mm});
            skLineSegment(sketch, "E26.7.0.0", {"start": v(-36.97, -157.5) * mm, "end": v(-20.25, -157.5) * mm});
            skPoint(sketch, "E26.7.0.1", {"position": v(-28.61, -149.38) * mm});
            skLineSegment(sketch, "E26.7.0.2", {"start": v(-36.97, -141.25) * mm, "end": v(-20.25, -141.25) * mm});
            skLineSegment(sketch, "E26.7.0.3", {"start": v(-20.25, -141.25) * mm, "end": v(-20.25, -157.5) * mm});
            skLineSegment(sketch, "E26.7.0.4", {"start": v(-36.97, -141.25) * mm, "end": v(-36.97, -157.5) * mm});
            skLineSegment(sketch, "E26.8.0.0", {"start": v(-17.95, -157.5) * mm, "end": v(-1.23, -157.5) * mm});
            skPoint(sketch, "E26.8.0.1", {"position": v(-9.6, -149.38) * mm});
            skLineSegment(sketch, "E26.8.0.2", {"start": v(-17.95, -141.25) * mm, "end": v(-1.23, -141.25) * mm});
            skLineSegment(sketch, "E26.8.0.3", {"start": v(-1.23, -141.25) * mm, "end": v(-1.23, -157.5) * mm});
            skLineSegment(sketch, "E26.8.0.4", {"start": v(-17.95, -141.25) * mm, "end": v(-17.95, -157.5) * mm});
            skLineSegment(sketch, "E26.9.0.0", {"start": v(1.07, -157.5) * mm, "end": v(17.79, -157.5) * mm});
            skPoint(sketch, "E26.9.0.1", {"position": v(9.43, -149.38) * mm});
            skLineSegment(sketch, "E26.9.0.2", {"start": v(1.07, -141.25) * mm, "end": v(17.79, -141.25) * mm});
            skLineSegment(sketch, "E26.9.0.3", {"start": v(17.79, -141.25) * mm, "end": v(17.79, -157.5) * mm});
            skLineSegment(sketch, "E26.9.0.4", {"start": v(1.07, -141.25) * mm, "end": v(1.07, -157.5) * mm});
            skLineSegment(sketch, "E26.10.0.0", {"start": v(20.09, -157.5) * mm, "end": v(36.8, -157.5) * mm});
            skPoint(sketch, "E26.10.0.1", {"position": v(28.45, -149.38) * mm});
            skLineSegment(sketch, "E26.10.0.2", {"start": v(20.09, -141.25) * mm, "end": v(36.8, -141.25) * mm});
            skLineSegment(sketch, "E26.10.0.3", {"start": v(36.8, -141.25) * mm, "end": v(36.8, -157.5) * mm});
            skLineSegment(sketch, "E26.10.0.4", {"start": v(20.09, -141.25) * mm, "end": v(20.09, -157.5) * mm});
            skLineSegment(sketch, "E26.11.0.0", {"start": v(39.1, -157.5) * mm, "end": v(55.83, -157.5) * mm});
            skPoint(sketch, "E26.11.0.1", {"position": v(47.47, -149.38) * mm});
            skLineSegment(sketch, "E26.11.0.2", {"start": v(39.1, -141.25) * mm, "end": v(55.83, -141.25) * mm});
            skLineSegment(sketch, "E26.11.0.3", {"start": v(55.83, -141.25) * mm, "end": v(55.83, -157.5) * mm});
            skLineSegment(sketch, "E26.11.0.4", {"start": v(39.1, -141.25) * mm, "end": v(39.1, -157.5) * mm});
            skLineSegment(sketch, "E27.bottom", {"start": v(-203.41, -159.8) * mm, "end": v(-181.91, -159.8) * mm});
            skLineSegment(sketch, "E27.top", {"start": v(-203.41, -176.05) * mm, "end": v(-181.91, -176.05) * mm});
            skLineSegment(sketch, "E27.left", {"start": v(-203.41, -159.8) * mm, "end": v(-203.41, -176.05) * mm});
            skLineSegment(sketch, "E27.right", {"start": v(-181.91, -159.8) * mm, "end": v(-181.91, -176.05) * mm});
            skPoint(sketch, "E27.middle", {"position": v(-192.66, -167.93) * mm});
            skLineSegment(sketch, "E28.bottom", {"start": v(-179.61, -159.8) * mm, "end": v(-162.9, -159.8) * mm});
            skLineSegment(sketch, "E28.top", {"start": v(-179.61, -176.05) * mm, "end": v(-162.9, -176.05) * mm});
            skLineSegment(sketch, "E28.left", {"start": v(-179.61, -159.8) * mm, "end": v(-179.61, -176.05) * mm});
            skLineSegment(sketch, "E28.right", {"start": v(-162.9, -159.8) * mm, "end": v(-162.9, -176.05) * mm});
            skPoint(sketch, "E28.middle", {"position": v(-171.25, -167.93) * mm});
            skLineSegment(sketch, "E29.1.0.0", {"start": v(-160.6, -159.8) * mm, "end": v(-160.6, -176.05) * mm});
            skLineSegment(sketch, "E29.1.0.1", {"start": v(-143.87, -159.8) * mm, "end": v(-143.87, -176.05) * mm});
            skLineSegment(sketch, "E29.1.0.2", {"start": v(-160.6, -176.05) * mm, "end": v(-143.87, -176.05) * mm});
            skPoint(sketch, "E29.1.0.3", {"position": v(-152.23, -167.93) * mm});
            skLineSegment(sketch, "E29.1.0.4", {"start": v(-160.6, -159.8) * mm, "end": v(-143.87, -159.8) * mm});
            skLineSegment(sketch, "E29.2.0.0", {"start": v(-141.57, -159.8) * mm, "end": v(-141.57, -176.05) * mm});
            skLineSegment(sketch, "E29.2.0.1", {"start": v(-124.85, -159.8) * mm, "end": v(-124.85, -176.05) * mm});
            skLineSegment(sketch, "E29.2.0.2", {"start": v(-141.57, -176.05) * mm, "end": v(-124.85, -176.05) * mm});
            skPoint(sketch, "E29.2.0.3", {"position": v(-133.21, -167.93) * mm});
            skLineSegment(sketch, "E29.2.0.4", {"start": v(-141.57, -159.8) * mm, "end": v(-124.85, -159.8) * mm});
            skLineSegment(sketch, "E29.3.0.0", {"start": v(-122.55, -159.8) * mm, "end": v(-122.55, -176.05) * mm});
            skLineSegment(sketch, "E29.3.0.1", {"start": v(-105.83, -159.8) * mm, "end": v(-105.83, -176.05) * mm});
            skLineSegment(sketch, "E29.3.0.2", {"start": v(-122.55, -176.05) * mm, "end": v(-105.83, -176.05) * mm});
            skPoint(sketch, "E29.3.0.3", {"position": v(-114.2, -167.93) * mm});
            skLineSegment(sketch, "E29.3.0.4", {"start": v(-122.55, -159.8) * mm, "end": v(-105.83, -159.8) * mm});
            skLineSegment(sketch, "E29.4.0.0", {"start": v(-103.53, -159.8) * mm, "end": v(-103.53, -176.05) * mm});
            skLineSegment(sketch, "E29.4.0.1", {"start": v(-86.81, -159.8) * mm, "end": v(-86.81, -176.05) * mm});
            skLineSegment(sketch, "E29.4.0.2", {"start": v(-103.53, -176.05) * mm, "end": v(-86.81, -176.05) * mm});
            skPoint(sketch, "E29.4.0.3", {"position": v(-95.17, -167.93) * mm});
            skLineSegment(sketch, "E29.4.0.4", {"start": v(-103.53, -159.8) * mm, "end": v(-86.81, -159.8) * mm});
            skLineSegment(sketch, "E29.5.0.0", {"start": v(-84.51, -159.8) * mm, "end": v(-84.51, -176.05) * mm});
            skLineSegment(sketch, "E29.5.0.1", {"start": v(-67.8, -159.8) * mm, "end": v(-67.8, -176.05) * mm});
            skLineSegment(sketch, "E29.5.0.2", {"start": v(-84.51, -176.05) * mm, "end": v(-67.8, -176.05) * mm});
            skPoint(sketch, "E29.5.0.3", {"position": v(-76.15, -167.93) * mm});
            skLineSegment(sketch, "E29.5.0.4", {"start": v(-84.51, -159.8) * mm, "end": v(-67.8, -159.8) * mm});
            skLineSegment(sketch, "E29.6.0.0", {"start": v(-65.5, -159.8) * mm, "end": v(-65.5, -176.05) * mm});
            skLineSegment(sketch, "E29.6.0.1", {"start": v(-48.77, -159.8) * mm, "end": v(-48.77, -176.05) * mm});
            skLineSegment(sketch, "E29.6.0.2", {"start": v(-65.5, -176.05) * mm, "end": v(-48.77, -176.05) * mm});
            skPoint(sketch, "E29.6.0.3", {"position": v(-57.13, -167.93) * mm});
            skLineSegment(sketch, "E29.6.0.4", {"start": v(-65.5, -159.8) * mm, "end": v(-48.77, -159.8) * mm});
            skLineSegment(sketch, "E29.7.0.0", {"start": v(-46.47, -159.8) * mm, "end": v(-46.47, -176.05) * mm});
            skLineSegment(sketch, "E29.7.0.1", {"start": v(-29.75, -159.8) * mm, "end": v(-29.75, -176.05) * mm});
            skLineSegment(sketch, "E29.7.0.2", {"start": v(-46.47, -176.05) * mm, "end": v(-29.75, -176.05) * mm});
            skPoint(sketch, "E29.7.0.3", {"position": v(-38.11, -167.93) * mm});
            skLineSegment(sketch, "E29.7.0.4", {"start": v(-46.47, -159.8) * mm, "end": v(-29.75, -159.8) * mm});
            skLineSegment(sketch, "E29.8.0.0", {"start": v(-27.45, -159.8) * mm, "end": v(-27.45, -176.05) * mm});
            skLineSegment(sketch, "E29.8.0.1", {"start": v(-10.73, -159.8) * mm, "end": v(-10.73, -176.05) * mm});
            skLineSegment(sketch, "E29.8.0.2", {"start": v(-27.45, -176.05) * mm, "end": v(-10.73, -176.05) * mm});
            skPoint(sketch, "E29.8.0.3", {"position": v(-19.1, -167.93) * mm});
            skLineSegment(sketch, "E29.8.0.4", {"start": v(-27.45, -159.8) * mm, "end": v(-10.73, -159.8) * mm});
            skLineSegment(sketch, "E29.9.0.0", {"start": v(-8.43, -159.8) * mm, "end": v(-8.43, -176.05) * mm});
            skLineSegment(sketch, "E29.9.0.1", {"start": v(8.29, -159.8) * mm, "end": v(8.29, -176.05) * mm});
            skLineSegment(sketch, "E29.9.0.2", {"start": v(-8.43, -176.05) * mm, "end": v(8.29, -176.05) * mm});
            skPoint(sketch, "E29.9.0.3", {"position": v(-0.07, -167.93) * mm});
            skLineSegment(sketch, "E29.9.0.4", {"start": v(-8.43, -159.8) * mm, "end": v(8.29, -159.8) * mm});
            skLineSegment(sketch, "E29.10.0.0", {"start": v(10.59, -159.8) * mm, "end": v(10.59, -176.05) * mm});
            skLineSegment(sketch, "E29.10.0.1", {"start": v(27.3, -159.8) * mm, "end": v(27.3, -176.05) * mm});
            skLineSegment(sketch, "E29.10.0.2", {"start": v(10.59, -176.05) * mm, "end": v(27.3, -176.05) * mm});
            skPoint(sketch, "E29.10.0.3", {"position": v(18.95, -167.93) * mm});
            skLineSegment(sketch, "E29.10.0.4", {"start": v(10.59, -159.8) * mm, "end": v(27.3, -159.8) * mm});
            skLineSegment(sketch, "E30.bottom", {"start": v(29.6, -159.8) * mm, "end": v(70.05, -159.8) * mm});
            skLineSegment(sketch, "E30.top", {"start": v(29.6, -176.05) * mm, "end": v(70.05, -176.05) * mm});
            skLineSegment(sketch, "E30.left", {"start": v(29.6, -159.8) * mm, "end": v(29.6, -176.05) * mm});
            skLineSegment(sketch, "E30.right", {"start": v(70.05, -159.8) * mm, "end": v(70.05, -176.05) * mm});
            skPoint(sketch, "E30.middle", {"position": v(49.83, -167.93) * mm});
            skLineSegment(sketch, "E31", {"start": v(70.05, -122.7) * mm, "end": v(70.05, -157.5) * mm});
            skLineSegment(sketch, "E32", {"start": v(70.05, -157.5) * mm, "end": v(58.13, -157.5) * mm});
            skLineSegment(sketch, "E33", {"start": v(58.13, -157.5) * mm, "end": v(58.13, -138.95) * mm});
            skLineSegment(sketch, "E34", {"start": v(58.13, -138.95) * mm, "end": v(53.38, -138.95) * mm});
            skLineSegment(sketch, "E35", {"start": v(53.38, -138.95) * mm, "end": v(53.38, -122.7) * mm});
            skLineSegment(sketch, "E36", {"start": v(53.38, -122.7) * mm, "end": v(70.05, -122.7) * mm});
            skLineSegment(sketch, "E37.bottom", {"start": v(-203.41, -178.35) * mm, "end": v(-177.16, -178.35) * mm});
            skLineSegment(sketch, "E37.top", {"start": v(-203.41, -197.25) * mm, "end": v(-177.16, -197.25) * mm});
            skLineSegment(sketch, "E37.left", {"start": v(-203.41, -178.35) * mm, "end": v(-203.41, -197.25) * mm});
            skLineSegment(sketch, "E37.right", {"start": v(-177.16, -178.35) * mm, "end": v(-177.16, -197.25) * mm});
            skPoint(sketch, "E37.middle", {"position": v(-190.29, -187.8) * mm});
            skLineSegment(sketch, "E38.bottom", {"start": v(-174.86, -178.35) * mm, "end": v(-153.36, -178.35) * mm});
            skLineSegment(sketch, "E38.top", {"start": v(-174.86, -197.25) * mm, "end": v(-153.36, -197.25) * mm});
            skLineSegment(sketch, "E38.left", {"start": v(-174.86, -178.35) * mm, "end": v(-174.86, -197.25) * mm});
            skLineSegment(sketch, "E38.right", {"start": v(-153.36, -178.35) * mm, "end": v(-153.36, -197.25) * mm});
            skPoint(sketch, "E38.middle", {"position": v(-164.11, -187.8) * mm});
            skLineSegment(sketch, "E39.bottom", {"start": v(-151.06, -178.35) * mm, "end": v(-124.81, -178.35) * mm});
            skLineSegment(sketch, "E39.top", {"start": v(-151.06, -197.25) * mm, "end": v(-124.81, -197.25) * mm});
            skLineSegment(sketch, "E39.left", {"start": v(-151.06, -178.35) * mm, "end": v(-151.06, -197.25) * mm});
            skLineSegment(sketch, "E39.right", {"start": v(-124.81, -178.35) * mm, "end": v(-124.81, -197.25) * mm});
            skPoint(sketch, "E39.middle", {"position": v(-137.94, -187.8) * mm});
            skLineSegment(sketch, "E40.bottom", {"start": v(-122.51, -178.35) * mm, "end": v(-10.81, -178.35) * mm});
            skLineSegment(sketch, "E40.top", {"start": v(-122.51, -197.25) * mm, "end": v(-10.81, -197.25) * mm});
            skLineSegment(sketch, "E40.left", {"start": v(-122.51, -178.35) * mm, "end": v(-122.51, -197.25) * mm});
            skLineSegment(sketch, "E40.right", {"start": v(-10.81, -178.35) * mm, "end": v(-10.81, -197.25) * mm});
            skPoint(sketch, "E40.middle", {"position": v(-66.66, -187.8) * mm});
            skLineSegment(sketch, "E41.1.0.0", {"start": v(-8.51, -178.35) * mm, "end": v(17.74, -178.35) * mm});
            skLineSegment(sketch, "E41.1.0.1", {"start": v(-8.51, -197.25) * mm, "end": v(17.74, -197.25) * mm});
            skLineSegment(sketch, "E41.1.0.2", {"start": v(41.54, -178.35) * mm, "end": v(41.54, -197.25) * mm});
            skPoint(sketch, "E41.1.0.3", {"position": v(4.61, -187.8) * mm});
            skLineSegment(sketch, "E41.1.0.4", {"start": v(20.04, -178.35) * mm, "end": v(41.54, -178.35) * mm});
            skLineSegment(sketch, "E41.1.0.5", {"start": v(20.04, -197.25) * mm, "end": v(41.54, -197.25) * mm});
            skLineSegment(sketch, "E41.1.0.6", {"start": v(17.74, -178.35) * mm, "end": v(17.74, -197.25) * mm});
            skLineSegment(sketch, "E41.1.0.7", {"start": v(20.04, -178.35) * mm, "end": v(20.04, -197.25) * mm});
            skLineSegment(sketch, "E41.1.0.8", {"start": v(43.84, -178.35) * mm, "end": v(70.09, -178.35) * mm});
            skLineSegment(sketch, "E41.1.0.9", {"start": v(70.09, -178.35) * mm, "end": v(70.09, -197.25) * mm});
            skPoint(sketch, "E41.1.0.10", {"position": v(30.79, -187.8) * mm});
            skPoint(sketch, "E41.1.0.11", {"position": v(56.96, -187.8) * mm});
            skLineSegment(sketch, "E41.1.0.12", {"start": v(43.84, -197.25) * mm, "end": v(70.09, -197.25) * mm});
            skLineSegment(sketch, "E41.1.0.13", {"start": v(43.84, -178.35) * mm, "end": v(43.84, -197.25) * mm});
            skLineSegment(sketch, "E41.1.0.14", {"start": v(-8.51, -178.35) * mm, "end": v(-8.51, -197.25) * mm});
            skLineSegment(sketch, "E42.bottom", {"start": v(-214.41, -80.25) * mm, "end": v(229.59, -80.25) * mm});
            skLineSegment(sketch, "E42.top", {"start": v(-214.41, -208.25) * mm, "end": v(229.59, -208.25) * mm});
            skLineSegment(sketch, "E42.left", {"start": v(-214.41, -80.25) * mm, "end": v(-214.41, -208.25) * mm});
            skLineSegment(sketch, "E42.right", {"start": v(229.59, -80.25) * mm, "end": v(229.59, -208.25) * mm});
            skSolve(sketch);
        }
        {
            var Q0;
            Q0=makeQuery(id+"F0.imprint","IMPRINT",FACE,{"disambiguationData":[TD([[makeQuery(id+"F0.imprint","IMPRINT",EDGE,{"derivedFrom":sQuery(id+"F0.wireOp",EDGE,"E0.bottom")}),-1.0]])]});
            var Q1;
            Q1=makeQuery(id+"F0.imprint","IMPRINT",FACE,{"disambiguationData":[TD([[makeQuery(id+"F0.imprint","IMPRINT",EDGE,{"derivedFrom":sQuery(id+"F0.wireOp",EDGE,"E1.bottom")}),1.0]])]});
            extrude(context, id + "F1", {"entities" : qUnion([Q0, Q1]), "depth" : 4 * mm, "offsetDistance" : 25 * mm});
        }
    });
